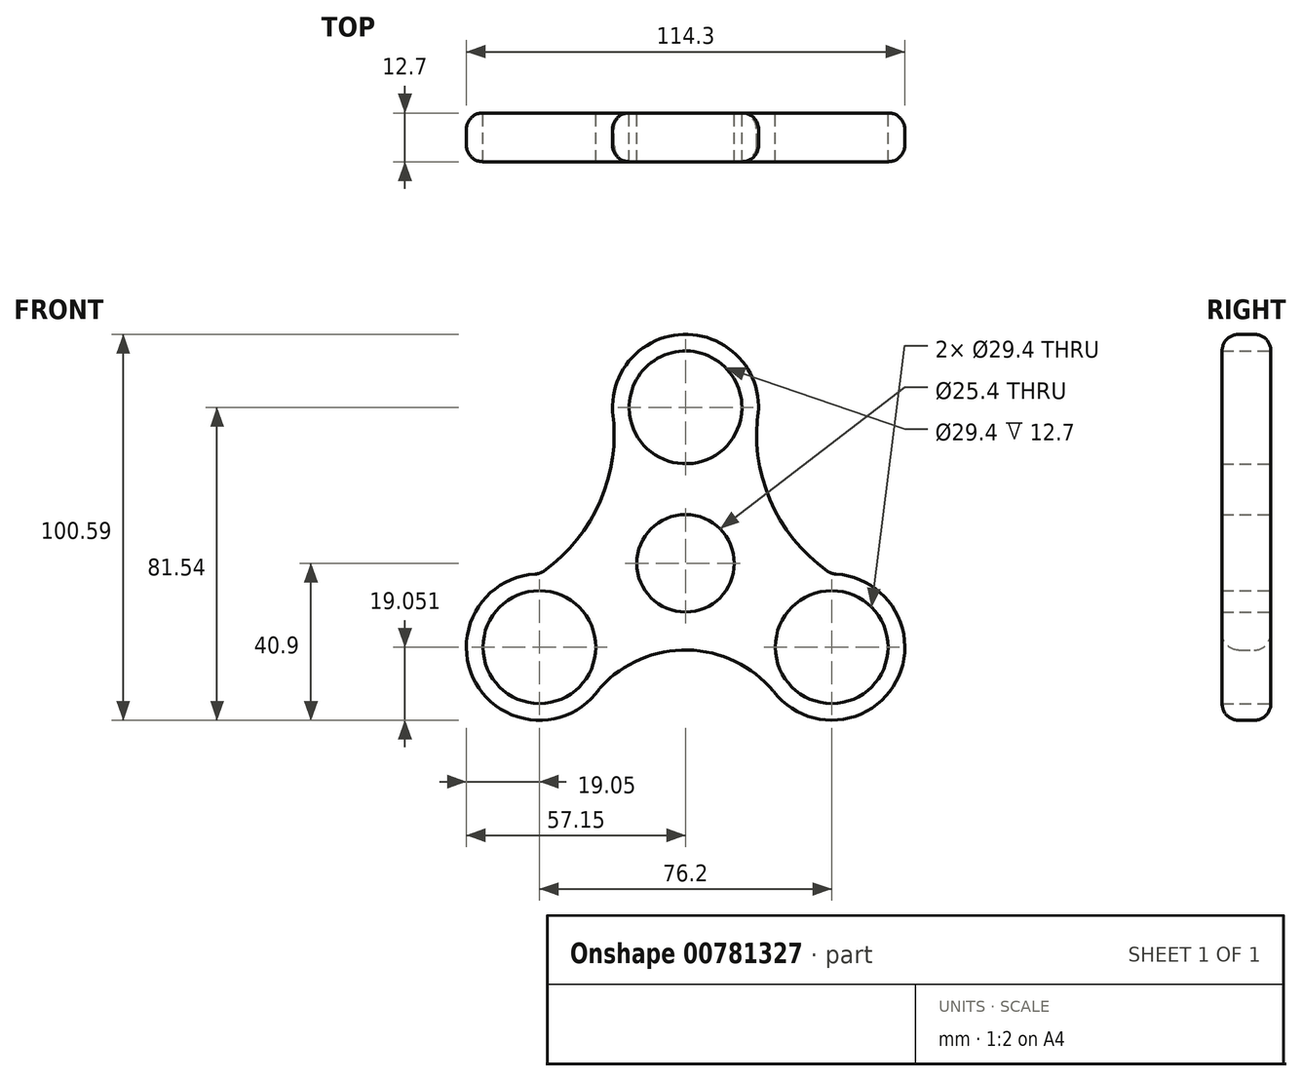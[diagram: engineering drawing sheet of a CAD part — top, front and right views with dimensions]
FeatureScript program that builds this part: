
annotation { "Feature Type Name" : "Feature", "Feature Type Description" : "" }
export const myFeature = defineFeature(function(context is Context, id is Id, definition is map)
    precondition{}
    {
        {
            var Q0;
            Q0=qCreatedBy(makeId("Front.planeOp"),FACE);
            var sketch = newSketch(context, id + "F0", { "sketchPlane" : qUnion([Q0])});
            skCircle(sketch, "E0", {"center": v(0, 0) * mm, "radius": 12.7 * mm});
            skCircle(sketch, "E1", {"center": v(0, 40.64) * mm, "radius": 14.7 * mm});
            skCircle(sketch, "E2", {"center": v(38.1, -21.85) * mm, "radius": 14.7 * mm});
            skCircle(sketch, "E3", {"center": v(-38.1, -21.85) * mm, "radius": 14.7 * mm});
            skCircle(sketch, "E4", {"center": v(-38.1, -21.85) * mm, "radius": 19.05 * mm});
            skCircle(sketch, "E5", {"center": v(38.1, -21.85) * mm, "radius": 19.05 * mm});
            skCircle(sketch, "E6", {"center": v(0, 40.64) * mm, "radius": 19.05 * mm});
            skPoint(sketch, "E7.visualSharp", {"position": v(0, -12.7) * mm});
            skArc(sketch, "E8", {"start": v(22.94, -33.38) * mm, "mid": v(0.5, -22.61) * mm, "end": v(-22.33, -32.54) * mm});
            skArc(sketch, "E9", {"start": v(-38.1, -2.8) * mm, "mid": v(-22.45, 15.67) * mm, "end": v(-19.02, 39.64) * mm});
            skArc(sketch, "E10", {"start": v(19.05, 40.64) * mm, "mid": v(22.18, 16.12) * mm, "end": v(38.1, -2.8) * mm});
            skSolve(sketch);
        }
        {
            var Q0;
            Q0=makeQuery(id+"F0.imprint","IMPRINT",FACE,{"disambiguationData":[TD([[makeQuery(id+"F0.imprint","IMPRINT",EDGE,{"derivedFrom":sQuery(id+"F0.wireOp",EDGE,"E3")}),-1.0]])]});
            var Q1;
            Q1=makeQuery(id+"F0.imprint","IMPRINT",FACE,{"disambiguationData":[TD([[makeQuery(id+"F0.imprint","IMPRINT",EDGE,{"derivedFrom":sQuery(id+"F0.wireOp",EDGE,"E2")}),-1.0]])]});
            var Q2;
            Q2=makeQuery(id+"F0.imprint","IMPRINT",FACE,{"disambiguationData":[TD([[makeQuery(id+"F0.imprint","IMPRINT",EDGE,{"derivedFrom":sQuery(id+"F0.wireOp",EDGE,"E0")}),-1.0]])]});
            var Q3;
            Q3=makeQuery(id+"F0.imprint","IMPRINT",FACE,{"disambiguationData":[TD([[makeQuery(id+"F0.imprint","IMPRINT",EDGE,{"derivedFrom":sQuery(id+"F0.wireOp",EDGE,"E1")}),-1.0]])]});
            extrude(context, id + "F1", {"entities" : qUnion([Q0, Q1, Q2, Q3]), "depth" : 12.7 * mm, "offsetDistance" : 25.4 * mm});
        }
        {
            var Q0;
            Q0=makeQuery(id+"F1.opExtrude","SWEPT_FACE",FACE,{"disambiguationData":[OSD([sQuery(id+"F0.wireOp",EDGE,"E8")])]});
            var Q1;
            Q1=makeQuery(id+"F1.opExtrude","SWEPT_FACE",FACE,{"disambiguationData":[OSD([sQuery(id+"F0.wireOp",EDGE,"E10")])]});
            var Q2;
            Q2=makeQuery(id+"F1.opExtrude","SWEPT_FACE",FACE,{"disambiguationData":[OSD([sQuery(id+"F0.wireOp",EDGE,"E9")])]});
            var Q3;
            Q3=makeQuery(id+"F1.opExtrude","SWEPT_FACE",FACE,{"disambiguationData":[OSD([sQuery(id+"F0.wireOp",EDGE,"E6")])]});
            var Q4;
            Q4=makeQuery(id+"F1.opExtrude","SWEPT_FACE",FACE,{"disambiguationData":[OSD([sQuery(id+"F0.wireOp",EDGE,"E5")])]});
            var Q5;
            Q5=makeQuery(id+"F1.opExtrude","SWEPT_FACE",FACE,{"disambiguationData":[OSD([sQuery(id+"F0.wireOp",EDGE,"E4")])]});
            fillet(context, id + "F2", {"entities" : qUnion([Q0, Q1, Q2, Q3, Q4, Q5]), "radius" : 4.3 * mm, "tangentPropagation" : true, "allowEdgeOverflow" : false});
        }
    });
